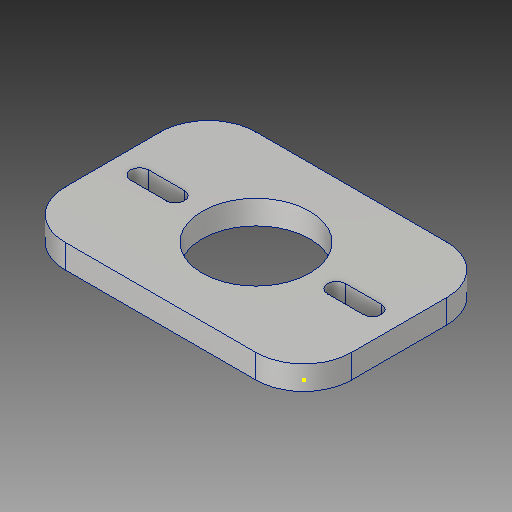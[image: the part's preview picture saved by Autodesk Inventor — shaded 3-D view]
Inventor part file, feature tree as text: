
AUTODESK INVENTOR PART (.ipt)
format: ipt  version: 2018 (Build 220112000, 112)  size: 139,776 bytes
history: native  units: in
note: dims shown in document units (in); Inventor stores cm internally (conversion verified against a paired STEP export)
features: sketch x4, extrude x2, hole x1, fillet x1
ambient origin geometry x8: Origin, YZ Plane, XZ Plane, XY Plane, X Axis, Y Axis, Z Axis, Center Point
bodies: Solid1 (feature_tree)
feature tree (8):
  extrude  "Extrusion1"  Depth=2.0in
  hole  "Hole1"  [1 undecoded]
  extrude  "Extrusion2"  Depth=0.1875in
  sketch  "Sketch4"  dims[d14=0.1875in d15=0.1875in d16=0.25in d17=0.0in d18=0.5in]
  fillet  "Fillet1"  Radius=0.1875in
  sketch  "Sketch1"  dims[d0=3.0in d1=2.0in]
  sketch  "Sketch2"  dims[d2=0.25in d3=0.0in d4=1.125in]
  sketch  "Sketch3"  dims[d5=1.125in d6=0.75in d7=0.375in d8=0.25in d9=0.5635in d10=1.0in d11=0.8108in d12=0.1875in d13=0.1875in]
note: 1 required parameter value undecoded (feature->parameter linkage not recoverable at this tier; creation-order binding heuristic only, values carry confidence <= 0.55)
